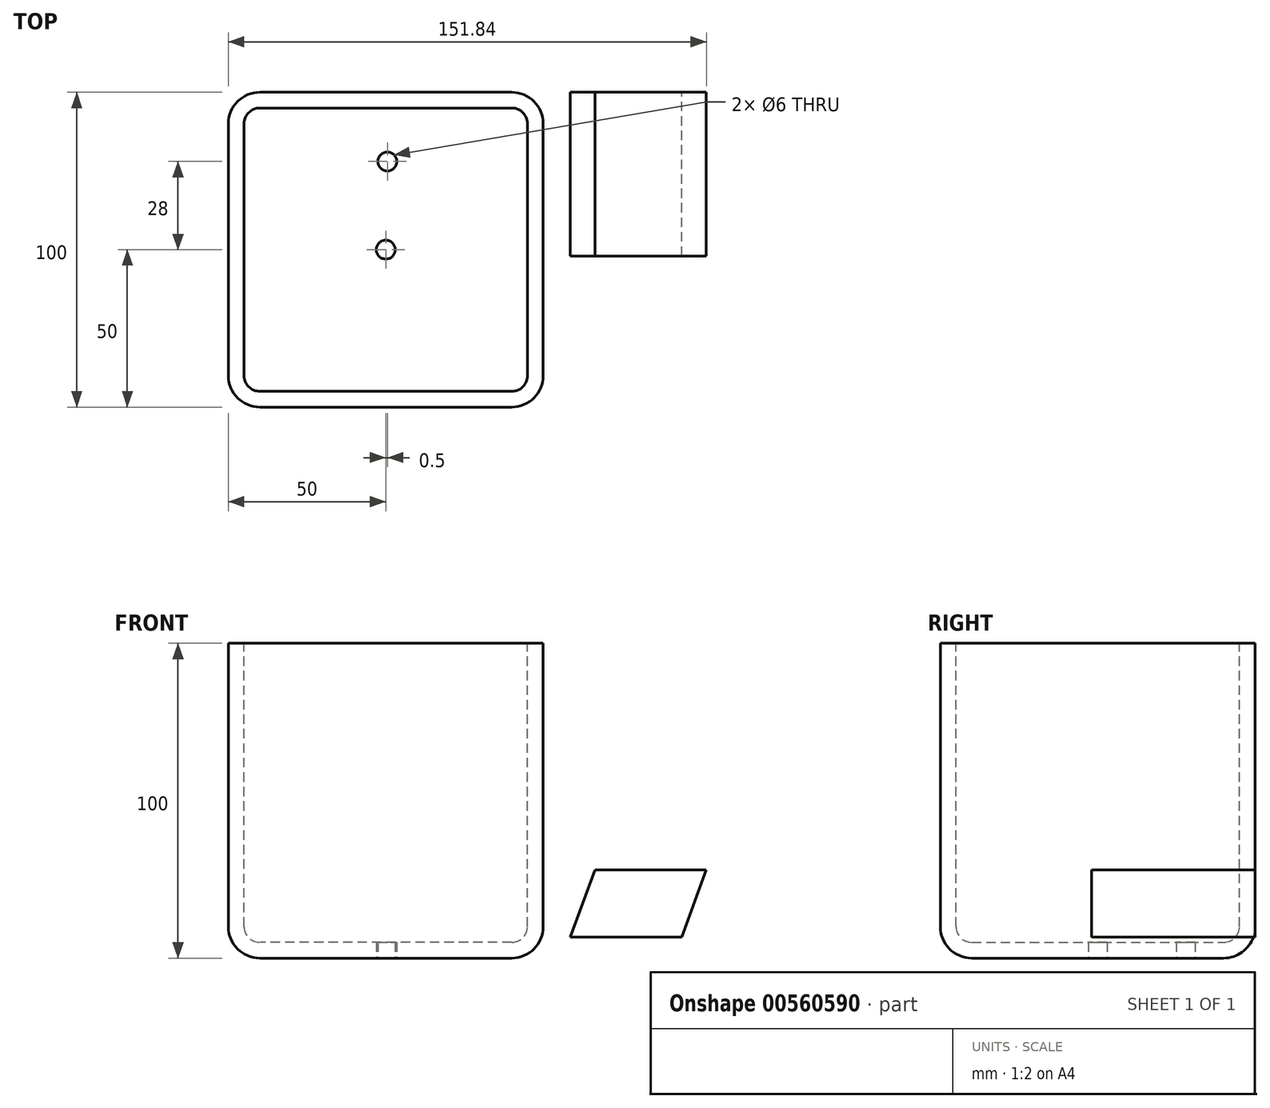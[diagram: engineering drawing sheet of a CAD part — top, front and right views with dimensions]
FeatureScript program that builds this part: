
annotation { "Feature Type Name" : "Feature", "Feature Type Description" : "" }
export const myFeature = defineFeature(function(context is Context, id is Id, definition is map)
    precondition{}
    {
        {
            var Q0;
            Q0=qCreatedBy(makeId("Front.planeOp"),FACE);
            var sketch = newSketch(context, id + "F0", { "sketchPlane" : qUnion([Q0])});
            skLineSegment(sketch, "E0", {"start": v(8.56, 6.74) * mm, "end": v(16.42, 28.07) * mm});
            skLineSegment(sketch, "E1", {"start": v(16.42, 28.07) * mm, "end": v(51.84, 28.07) * mm});
            skLineSegment(sketch, "E2", {"start": v(51.84, 28.07) * mm, "end": v(43.98, 6.74) * mm});
            skLineSegment(sketch, "E3", {"start": v(43.98, 6.74) * mm, "end": v(8.56, 6.74) * mm});
            skSolve(sketch);
        }
        {
            var Q0;
            Q0 = qSketchRegion(id + "F0", true);
            extrude(context, id + "F1", {"entities" : qUnion([Q0]), "depth" : 52 * mm, "offsetDistance" : 25 * mm});
        }
        {
            var Q0;
            Q0=qCreatedBy(makeId("Front.planeOp"),FACE);
            var sketch = newSketch(context, id + "F2", { "sketchPlane" : qUnion([Q0])});
            skLineSegment(sketch, "E4.bottom", {"start": v(0, 0) * mm, "end": v(-100, 0) * mm});
            skLineSegment(sketch, "E4.top", {"start": v(0, 100) * mm, "end": v(-100, 100) * mm});
            skLineSegment(sketch, "E4.left", {"start": v(0, 0) * mm, "end": v(0, 100) * mm});
            skLineSegment(sketch, "E4.right", {"start": v(-100, 0) * mm, "end": v(-100, 100) * mm});
            skSolve(sketch);
        }
        {
            var Q0;
            Q0 = qSketchRegion(id + "F2", true);
            extrude(context, id + "F3", {"entities" : qUnion([Q0]), "depth" : 100 * mm, "offsetDistance" : 25 * mm});
        }
        {
            var Q0;
            Q0=makeQuery(id+"F3.opExtrude","CAP_EDGE",EDGE,{"disambiguationData":[OSD([sQuery(id+"F2.wireOp",EDGE,"E4.right")])],"isStart":true});
            var Q1;
            Q1=makeQuery(id+"F3.opExtrude","CAP_EDGE",EDGE,{"disambiguationData":[OSD([sQuery(id+"F2.wireOp",EDGE,"E4.right")])],"isStart":false});
            var Q2;
            Q2=makeQuery(id+"F3.opExtrude","CAP_EDGE",EDGE,{"disambiguationData":[OSD([sQuery(id+"F2.wireOp",EDGE,"E4.left")])],"isStart":true});
            var Q3;
            Q3=makeQuery(id+"F3.opExtrude","CAP_EDGE",EDGE,{"disambiguationData":[OSD([sQuery(id+"F2.wireOp",EDGE,"E4.left")])],"isStart":false});
            var Q4;
            Q4=makeQuery(id+"F3.opExtrude","CAP_EDGE",EDGE,{"disambiguationData":[OSD([sQuery(id+"F2.wireOp",EDGE,"E4.bottom")])],"isStart":false});
            var Q5;
            Q5=makeQuery(id+"F3.opExtrude","SWEPT_EDGE",EDGE,{"disambiguationData":[OSD([sQuery(id+"F2.wireOp",EDGE,"E4.bottom"),sQuery(id+"F2.wireOp",EDGE,"E4.right")])]});
            var Q6;
            Q6=makeQuery(id+"F3.opExtrude","CAP_EDGE",EDGE,{"disambiguationData":[OSD([sQuery(id+"F2.wireOp",EDGE,"E4.bottom")])],"isStart":true});
            var Q7;
            Q7=makeQuery(id+"F3.opExtrude","SWEPT_EDGE",EDGE,{"disambiguationData":[OSD([sQuery(id+"F2.wireOp",EDGE,"E4.bottom"),sQuery(id+"F2.wireOp",EDGE,"E4.left")])]});
            fillet(context, id + "F4", {"entities" : qUnion([Q0, Q1, Q2, Q3, Q4, Q5, Q6, Q7]), "radius" : 10 * mm, "tangentPropagation" : true, "allowEdgeOverflow" : false});
        }
        {
            var Q0;
            Q0=makeQuery(id+"F3.opExtrude","SWEPT_FACE",FACE,{"disambiguationData":[OSD([sQuery(id+"F2.wireOp",EDGE,"E4.top")])]});
            shell(context, id + "F5", {"entities" : qUnion([Q0]), "thickness" : 5 * mm});
        }
        {
            var Q0;
            Q0=makeQuery(id+"F3.opExtrude","SWEPT_FACE",FACE,{"disambiguationData":[OSD([sQuery(id+"F2.wireOp",EDGE,"E4.bottom")])]});
            var sketch = newSketch(context, id + "F6", { "sketchPlane" : qUnion([Q0])});
            skCircle(sketch, "E5", {"center": v(-50, 50) * mm, "radius": 3 * mm});
            skSolve(sketch);
        }
        {
            var Q0;
            Q0 = qSketchRegion(id + "F6", true);
            extrude(context, id + "F7", {"entities" : qUnion([Q0]), "operationType" : NewBodyOperationType.REMOVE, "oppositeDirection" : true, "depth" : 25 * mm, "offsetDistance" : 25 * mm});
        }
        {
            var Q0;
            Q0=makeQuery(id+"F3.opExtrude","SWEPT_FACE",FACE,{"disambiguationData":[OSD([sQuery(id+"F2.wireOp",EDGE,"E4.bottom")])]});
            var sketch = newSketch(context, id + "F8", { "sketchPlane" : qUnion([Q0])});
            skCircle(sketch, "E6", {"center": v(-49.5, 22) * mm, "radius": 3 * mm});
            skSolve(sketch);
        }
        {
            var Q0;
            Q0 = qSketchRegion(id + "F8", true);
            extrude(context, id + "F9", {"entities" : qUnion([Q0]), "operationType" : NewBodyOperationType.REMOVE, "oppositeDirection" : true, "depth" : 25 * mm, "offsetDistance" : 25 * mm});
        }
    });
